# Revit family: Оникс
name_source: partatom
category: Осветительные приборы
units: mm (PartAtom-declared; Revit-internal decimal feet)

## family parameters
Всегда вертикально = Да
Источник света = Да
На основе рабочей плоскости = Нет
Общий = Нет
При загрузке вырезать с полостями = Нет
Размер круглого соединителя = Использовать диаметр
Тип детали = Нормальный
Точка расчета площади = Нет

## types (1)
- ДТУ811 Светодиодный светильник Оникс ДТУ-81-AF-7Вт-0,4
    ADSK_URL страницы изделия = https://www.allfresco.ru
    ADSK_Артикул = ДТУ811
    ADSK_Единица измерения = шт.
    ADSK_Завод-изготовитель = ALFRESCO
    ADSK_Количество фаз = 2
    ADSK_Количество фаз числовое = 0
    ADSK_Коэффициент мощности = 0
    ADSK_Масса = 3
    ADSK_Масса_Текст = 3
    ADSK_Модель = Оникс ДТУ-81-AF
    ADSK_Наименование = ДТУ811 Светодиодный светильник Оникс ДТУ-81-AF-7Вт-0.4
    ADSK_Напряжение = 220 В
    ADSK_Номинальная мощность = 7 Вт
    ADSK_Полная мощность = 0 В·А
    ADSK_Размер_Высота = 400 мм
    ADSK_Ток = 0 А
    ADSK_Фактическая мощность = 7 Вт
    ADSK_Энергоэффективность = 100 лм/Вт
    H_конечной точки = 1500 мм
    IP Class = IP 67
    L_вырез = 200 мм
    L_отступ до конечной точки = 1500 мм
    L_отступ до центра = 1000 мм
    R_основание = 50 мм
    Блок аварийного питания = Нет
    Класс защиты = 1
    Класс пожароопасности = F (устройства предназначены для установки непосредственно на поверхность из нормально воспламеняемых материалов)
    Климатическая зона = УХЛ1
    Короб_Диаметр = 20 мм
    Корпус светильника = Сталь, окрашенная, темно-серая
    Материал рассеивателя = Светотехнический ПК
    Область использования = Парки, скверы, общественные пространства, городская инфраструктура
    Полная установленная мощность = 0 В·А
    Рассеиватель = Материал рассеивателя
    Светофильтр = 16777215
    Смещение цветовой температуры при затухании лампы = <Нет>
    Таблица выбора = Таблица параметров светильников_par4_v1
    Температура эксплуатации = -40 +50
    Тип ИС = LED-модуль
    Тип КСС = специальная
    Тип ПРА = -
    Тип продукции = LED-светильник
    Угол наклона = 90.00°
    Файл фотометрической сетки = DTU-81-AF Oniks 7W.ies
    Цветоывая температура = 2700-5500

## geometry (parser evidence)
native form markers: Blend x2
no freeform markers — native parametric forms only
